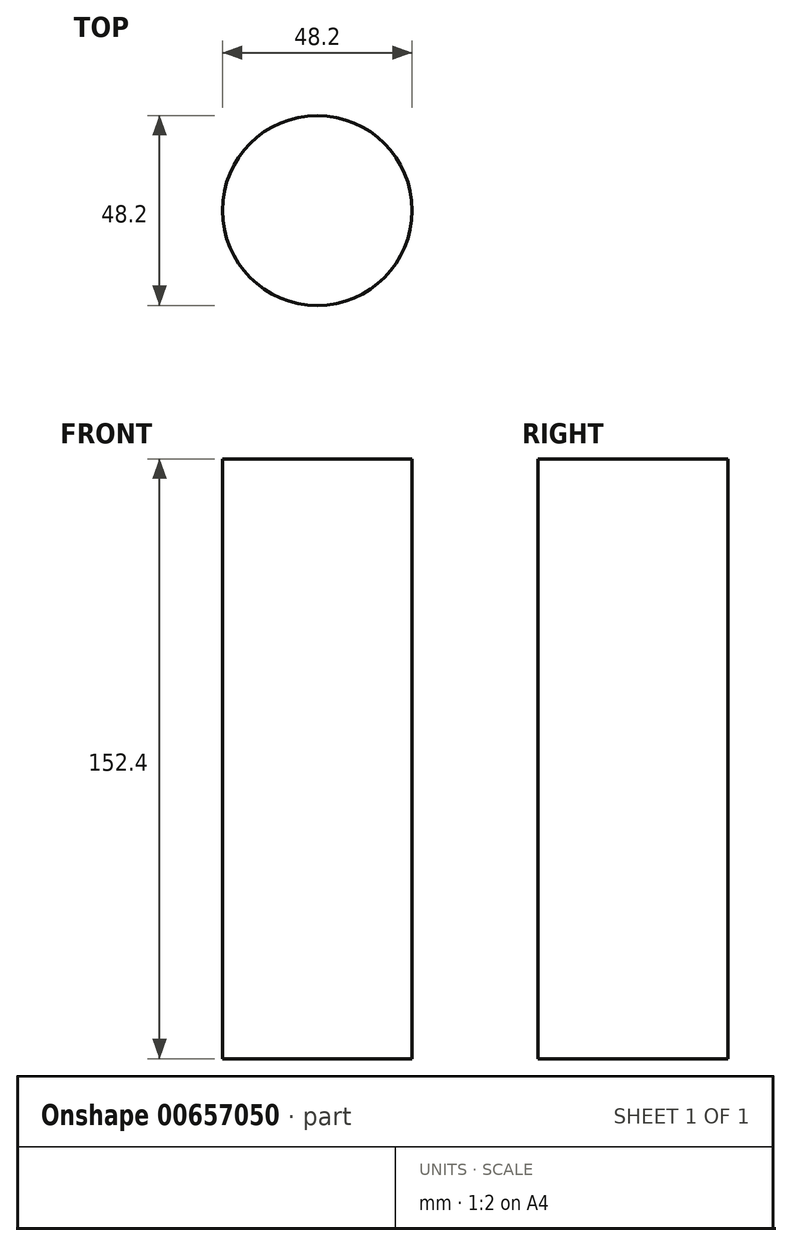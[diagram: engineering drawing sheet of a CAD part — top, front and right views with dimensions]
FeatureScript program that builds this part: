
annotation { "Feature Type Name" : "Feature", "Feature Type Description" : "" }
export const myFeature = defineFeature(function(context is Context, id is Id, definition is map)
    precondition{}
    {
        {
            var Q0;
            Q0=qCreatedBy(makeId("Top.planeOp"),FACE);
            var sketch = newSketch(context, id + "F0", { "sketchPlane" : qUnion([Q0])});
            skCircle(sketch, "E0", {"center": v(0, 0) * mm, "radius": 24.1 * mm});
            skCircle(sketch, "E1", {"center": v(0, 0) * mm, "radius": 35.07 * mm});
            skSolve(sketch);
        }
        {
            var Q0;
            Q0=makeQuery(id+"F0.imprint","IMPRINT",FACE,{"disambiguationData":[TD([[makeQuery(id+"F0.imprint","IMPRINT",EDGE,{"derivedFrom":sQuery(id+"F0.wireOp",EDGE,"E0")}),1.0]])]});
            extrude(context, id + "F1", {"entities" : qUnion([Q0]), "depth" : 152.4 * mm, "offsetDistance" : 25.4 * mm});
        }
        {
            var Q1;
            Q1=qCreatedBy(makeId("Origin.pointOp"),VERTEX);
            var Q2;
            Q2=makeQuery(id+"F1.opExtrude","CAP_FACE",FACE,{"disambiguationData":[OSD([sQuery(id+"F0.wireOp",EDGE,"E0")])],"isStart":false});
            loft(context, id + "F2", {"operationType" : NewBodyOperationType.ADD, "sheetProfilesArray" : [{ "sheetProfileEntities" : qUnion([Q1]) }, { "sheetProfileEntities" : qUnion([Q2]) }]});
        }
    });
